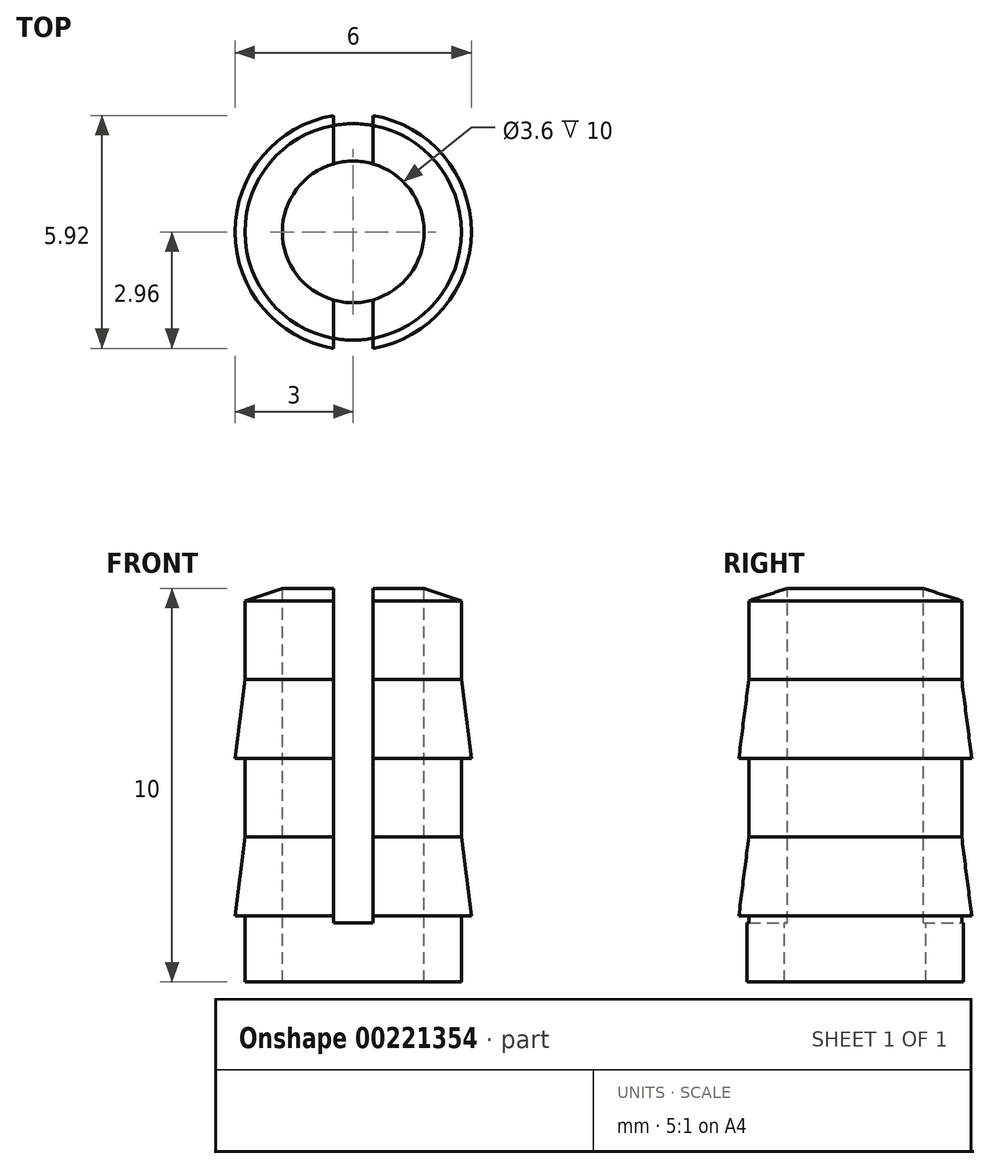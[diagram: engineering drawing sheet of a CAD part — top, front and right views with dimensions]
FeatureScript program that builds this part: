
annotation { "Feature Type Name" : "Feature", "Feature Type Description" : "" }
export const myFeature = defineFeature(function(context is Context, id is Id, definition is map)
    precondition{}
    {
        {
            var Q0;
            Q0=qCreatedBy(makeId("Front.planeOp"),FACE);
            var sketch = newSketch(context, id + "F0", { "sketchPlane" : qUnion([Q0])});
            skLineSegment(sketch, "E0", {"start": v(0, 5.11) * mm, "end": v(0, -4.38) * mm, "construction": true});
            skLineSegment(sketch, "E1", {"start": v(1.8, 10) * mm, "end": v(1.8, 0) * mm});
            skLineSegment(sketch, "E2", {"start": v(1.8, 0) * mm, "end": v(2.75, 0) * mm});
            skLineSegment(sketch, "E3", {"start": v(2.75, 0) * mm, "end": v(2.75, 1.69) * mm});
            skLineSegment(sketch, "E4", {"start": v(2.75, 1.69) * mm, "end": v(3, 1.69) * mm});
            skLineSegment(sketch, "E5", {"start": v(3, 1.69) * mm, "end": v(2.75, 3.69) * mm});
            skLineSegment(sketch, "E6", {"start": v(2.75, 3.69) * mm, "end": v(2.75, 5.69) * mm});
            skLineSegment(sketch, "E7", {"start": v(2.75, 5.69) * mm, "end": v(3, 5.69) * mm});
            skLineSegment(sketch, "E8", {"start": v(3, 5.69) * mm, "end": v(2.75, 7.69) * mm});
            skLineSegment(sketch, "E9", {"start": v(2.75, 7.69) * mm, "end": v(2.75, 9.69) * mm});
            skLineSegment(sketch, "E10", {"start": v(2.75, 9.69) * mm, "end": v(1.8, 10) * mm});
            skSolve(sketch);
        }
        {
            var Q0;
            Q0=makeQuery(id+"F0.imprint","IMPRINT",FACE,{"disambiguationData":[TD([[makeQuery(id+"F0.imprint","IMPRINT",EDGE,{"derivedFrom":sQuery(id+"F0.wireOp",EDGE,"E1")}),1.0]])]});
            var Q1;
            Q1=sQuery(id+"F0.wireOp",EDGE,"E0");
            revolve(context, id + "F1", {"surfaceOperationType" : NewSurfaceOperationType.NEW, "entities" : qUnion([Q0]), "axis" : qUnion([Q1]), "revolveType" : RevolveType.FULL});
        }
        {
            var Q0;
            Q0=qCreatedBy(makeId("Front.planeOp"),FACE);
            var sketch = newSketch(context, id + "F2", { "sketchPlane" : qUnion([Q0])});
            skLineSegment(sketch, "E11.0", {"start": v(-1.8, 10) * mm, "end": v(1.8, 10) * mm});
            skLineSegment(sketch, "E12", {"start": v(-0.5, 10) * mm, "end": v(-0.5, 1.5) * mm});
            skLineSegment(sketch, "E13", {"start": v(-0.5, 1.5) * mm, "end": v(0, 1.5) * mm});
            skLineSegment(sketch, "E14.MirrorCS", {"start": v(0.5, 10) * mm, "end": v(0.5, 1.5) * mm});
            skLineSegment(sketch, "E15.MirrorCS", {"start": v(0.5, 1.5) * mm, "end": v(0, 1.5) * mm});
            skSolve(sketch);
        }
        {
            var Q0;
            {var subQ1=sQuery(id+"F2.wireOp",EDGE,"E12");Q0=makeQuery(id+"F2.imprint","IMPRINT",FACE,{"disambiguationData":[TD([[makeQuery(id+"F2.imprint","IMPRINT",EDGE,{"derivedFrom":subQ1}),1.0]])]});}
            extrude(context, id + "F3", {"entities" : qUnion([Q0]), "operationType" : NewBodyOperationType.REMOVE, "depth" : 25 * mm, "offsetDistance" : 25 * mm, "symmetric" : true});
        }
    });
